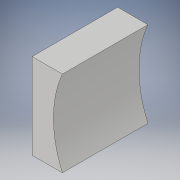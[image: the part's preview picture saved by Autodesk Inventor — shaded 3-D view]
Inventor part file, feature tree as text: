
AUTODESK INVENTOR PART (.ipt)
format: ipt  version: 2018.3 (Build 223284000, 284)  size: 99,328 bytes
history: native  units: in
note: dims shown in document units (in); Inventor stores cm internally (conversion verified against a paired STEP export)
features: extrude x2, sketch x2
ambient origin geometry x8: Origin, YZ Plane, XZ Plane, XY Plane, X Axis, Y Axis, Z Axis, Center Point
bodies: Solid1 (feature_tree)
feature tree (4):
  extrude  "Extrusion1"  Depth=1.0in
  extrude  "Extrusion2"  Depth=1.0in TaperAngle=0.0deg
  sketch  "Sketch1"  dims[d0=1.5in d1=1.0in]
  sketch  "Sketch2"  dims[d2=1.25in d3=1.0in d4=0.0in d5=1.25in d6=1.0in d7=0.0in]
